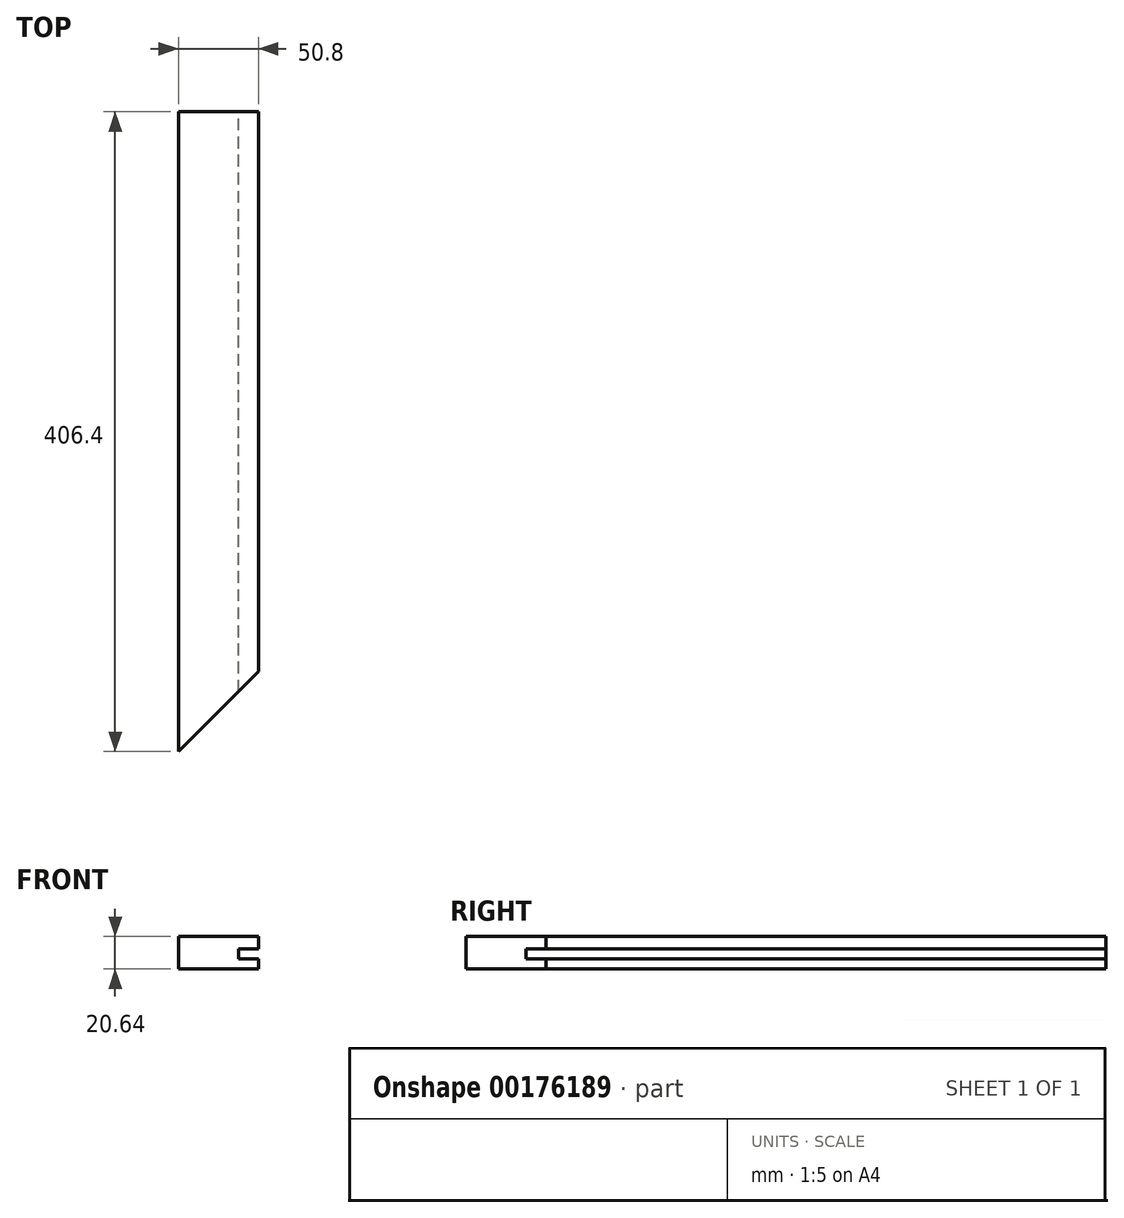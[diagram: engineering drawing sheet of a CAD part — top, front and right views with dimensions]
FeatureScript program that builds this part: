
annotation { "Feature Type Name" : "Feature", "Feature Type Description" : "" }
export const myFeature = defineFeature(function(context is Context, id is Id, definition is map)
    precondition{}
    {
        {
            var Q0;
            Q0=qCreatedBy(makeId("Top.planeOp"),FACE);
            var sketch = newSketch(context, id + "F0", { "sketchPlane" : qUnion([Q0])});
            skLineSegment(sketch, "E0.top", {"start": v(0, 406.4) * mm, "end": v(50.8, 406.4) * mm});
            skLineSegment(sketch, "E0.left", {"start": v(0, 0) * mm, "end": v(0, 406.4) * mm});
            skLineSegment(sketch, "E0.right", {"start": v(50.8, 50.8) * mm, "end": v(50.8, 406.4) * mm});
            skLineSegment(sketch, "E1", {"start": v(0, 0) * mm, "end": v(50.8, 50.8) * mm});
            skSolve(sketch);
        }
        {
            var Q0;
            Q0=makeQuery(id+"F0.imprint","IMPRINT",FACE,{"disambiguationData":[TD([[makeQuery(id+"F0.imprint","IMPRINT",EDGE,{"derivedFrom":sQuery(id+"F0.wireOp",EDGE,"E0.top")}),-1.0]])]});
            extrude(context, id + "F1", {"entities" : qUnion([Q0]), "depth" : 20.64 * mm});
        }
        {
            var Q0;
            Q0=makeQuery(id+"F1.opExtrude","SWEPT_FACE",FACE,{"disambiguationData":[OSD([sQuery(id+"F0.wireOp",EDGE,"E0.top")])]});
            var sketch = newSketch(context, id + "F2", { "sketchPlane" : qUnion([Q0])});
            skLineSegment(sketch, "E2.bottom", {"start": v(-50.8, 6.35) * mm, "end": v(-38.1, 6.35) * mm});
            skLineSegment(sketch, "E2.top", {"start": v(-50.8, 12.7) * mm, "end": v(-38.1, 12.7) * mm});
            skLineSegment(sketch, "E2.left", {"start": v(-50.8, 6.35) * mm, "end": v(-50.8, 12.7) * mm});
            skLineSegment(sketch, "E2.right", {"start": v(-38.1, 6.35) * mm, "end": v(-38.1, 12.7) * mm});
            skSolve(sketch);
        }
        {
            var Q0;
            Q0=makeQuery(id+"F2.imprint","IMPRINT",FACE,{"disambiguationData":[TD([[makeQuery(id+"F2.imprint","IMPRINT",EDGE,{"derivedFrom":sQuery(id+"F2.wireOp",EDGE,"E2.bottom")}),1.0]])]});
            extrude(context, id + "F3", {"entities" : qUnion([Q0]), "operationType" : NewBodyOperationType.REMOVE, "endBound" : BoundingType.THROUGH_ALL, "oppositeDirection" : true, "depth" : 25.4 * mm});
        }
    });
